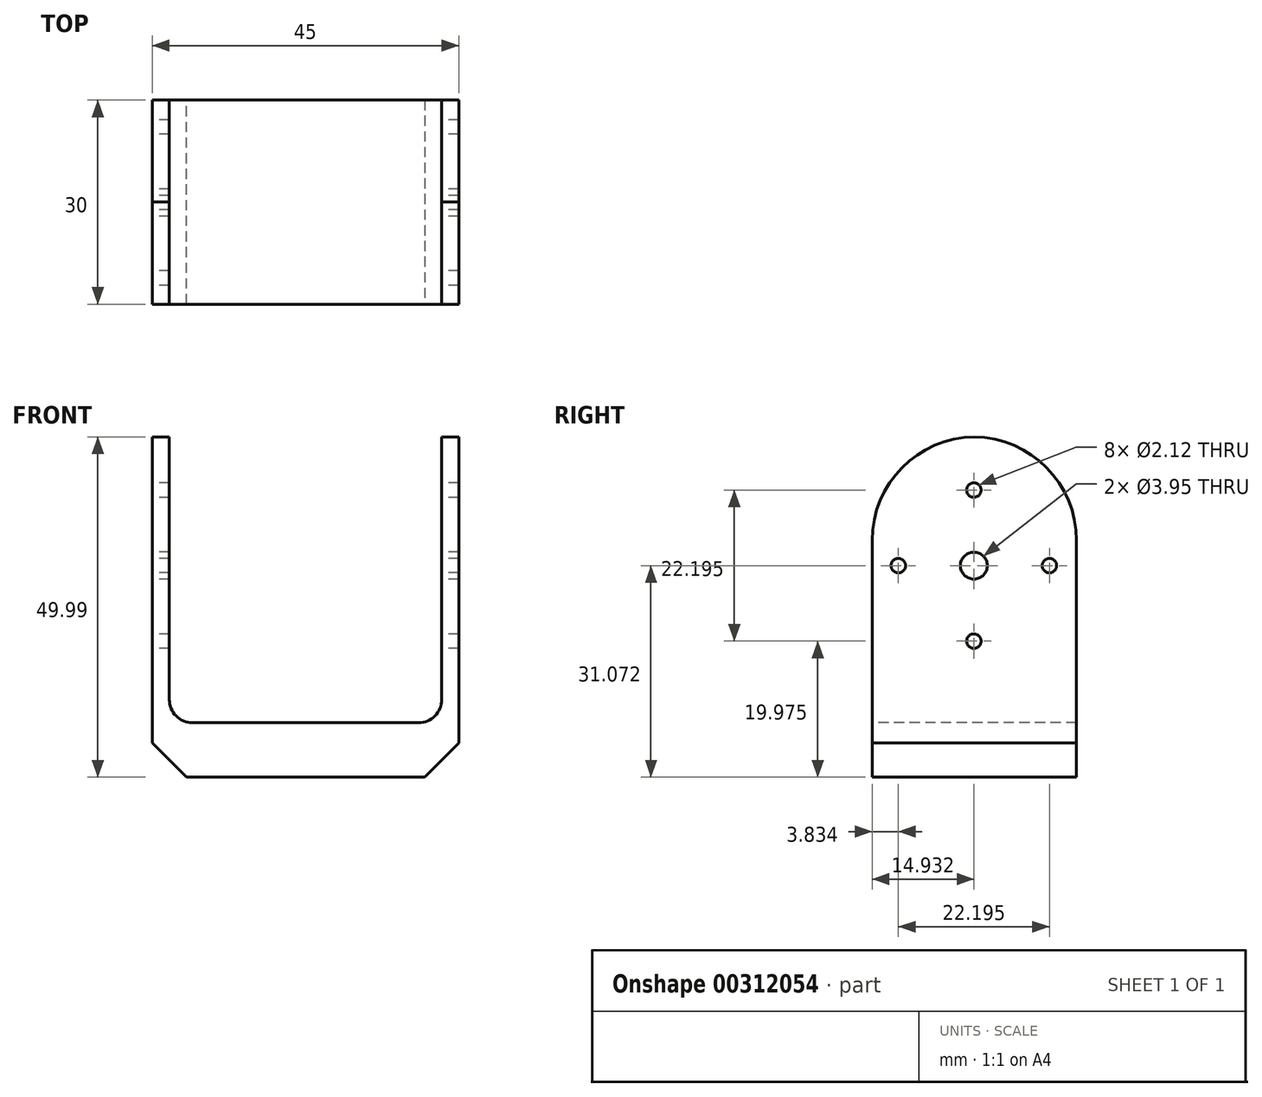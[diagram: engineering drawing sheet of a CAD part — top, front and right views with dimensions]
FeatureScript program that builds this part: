
annotation { "Feature Type Name" : "Feature", "Feature Type Description" : "" }
export const myFeature = defineFeature(function(context is Context, id is Id, definition is map)
    precondition{}
    {
        {
            var Q0;
            Q0=qCreatedBy(makeId("Front.planeOp"),FACE);
            var sketch = newSketch(context, id + "F0", { "sketchPlane" : qUnion([Q0])});
            skLineSegment(sketch, "E0.bottom", {"start": v(-16.8, 31.56) * mm, "end": v(28.2, 31.56) * mm});
            skLineSegment(sketch, "E0.top", {"start": v(-16.8, -18.44) * mm, "end": v(28.2, -18.44) * mm});
            skLineSegment(sketch, "E0.left", {"start": v(-16.8, 31.56) * mm, "end": v(-16.8, -18.44) * mm});
            skLineSegment(sketch, "E0.right", {"start": v(28.2, 31.56) * mm, "end": v(28.2, -18.44) * mm});
            skSolve(sketch);
        }
        {
            var Q0;
            Q0 = qSketchRegion(id + "F0", true);
            extrude(context, id + "F1", {"entities" : qUnion([Q0]), "depth" : 30 * mm});
        }
        {
            var Q0;
            Q0=makeQuery(id+"F1.opExtrude","CAP_FACE",FACE,{"disambiguationData":[OSD([sQuery(id+"F0.wireOp",EDGE,"E0.bottom"),sQuery(id+"F0.wireOp",EDGE,"E0.top"),sQuery(id+"F0.wireOp",EDGE,"E0.left"),sQuery(id+"F0.wireOp",EDGE,"E0.right")])],"isStart":false});
            var sketch = newSketch(context, id + "F2", { "sketchPlane" : qUnion([Q0])});
            skLineSegment(sketch, "E1.bottom", {"start": v(-14.3, 31.56) * mm, "end": v(25.7, 31.56) * mm, "construction": true});
            skLineSegment(sketch, "E1.top", {"start": v(-14.3, -10.44) * mm, "end": v(25.7, -10.44) * mm, "construction": true});
            skLineSegment(sketch, "E1.left", {"start": v(-14.3, 31.56) * mm, "end": v(-14.3, -10.44) * mm, "construction": true});
            skLineSegment(sketch, "E1.right", {"start": v(25.7, 31.56) * mm, "end": v(25.7, -10.44) * mm, "construction": true});
            skLineSegment(sketch, "E2.bottom", {"start": v(-14.3, 31.56) * mm, "end": v(25.7, 31.56) * mm});
            skLineSegment(sketch, "E2.top", {"start": v(-14.3, -10.44) * mm, "end": v(25.7, -10.44) * mm});
            skLineSegment(sketch, "E2.left", {"start": v(-14.3, 31.56) * mm, "end": v(-14.3, -10.44) * mm});
            skLineSegment(sketch, "E2.right", {"start": v(25.7, 31.56) * mm, "end": v(25.7, -10.44) * mm});
            skSolve(sketch);
        }
        {
            var Q0;
            Q0 = qSketchRegion(id + "F2", true);
            extrude(context, id + "F3", {"entities" : qUnion([Q0]), "operationType" : NewBodyOperationType.REMOVE, "endBound" : BoundingType.THROUGH_ALL, "oppositeDirection" : true, "depth" : 25 * mm});
        }
        {
            var Q0;
            {var subQ0=sQuery(id+"F0.wireOp",EDGE,"E0.bottom");var subQ1=sQuery(id+"F0.wireOp",EDGE,"E0.left");Q0=makeQuery(id+"F3.boolean.opBoolean","SPLIT",EDGE,{"disambiguationData":[TD([makeQuery(id+"F1.opExtrude","SWEPT_FACE",FACE,{"disambiguationData":[OSD([subQ1])]})])],"derivedFrom":makeQuery(id+"F1.opExtrude","CAP_EDGE",EDGE,{"disambiguationData":[OSD([subQ0])],"isStart":true})});}
            var Q1;
            {var subQ0=sQuery(id+"F0.wireOp",EDGE,"E0.bottom");var subQ1=sQuery(id+"F0.wireOp",EDGE,"E0.left");Q1=makeQuery(id+"F3.boolean.opBoolean","SPLIT",EDGE,{"disambiguationData":[TD([makeQuery(id+"F1.opExtrude","SWEPT_FACE",FACE,{"disambiguationData":[OSD([subQ1])]})])],"derivedFrom":makeQuery(id+"F1.opExtrude","CAP_EDGE",EDGE,{"disambiguationData":[OSD([subQ0])],"isStart":false})});}
            var Q2;
            {var subQ0=sQuery(id+"F0.wireOp",EDGE,"E0.bottom");var subQ1=sQuery(id+"F0.wireOp",EDGE,"E0.right");Q2=makeQuery(id+"F3.boolean.opBoolean","SPLIT",EDGE,{"disambiguationData":[TD([makeQuery(id+"F1.opExtrude","SWEPT_FACE",FACE,{"disambiguationData":[OSD([subQ1])]})])],"derivedFrom":makeQuery(id+"F1.opExtrude","CAP_EDGE",EDGE,{"disambiguationData":[OSD([subQ0])],"isStart":false})});}
            var Q3;
            {var subQ0=sQuery(id+"F0.wireOp",EDGE,"E0.bottom");var subQ1=sQuery(id+"F0.wireOp",EDGE,"E0.right");Q3=makeQuery(id+"F3.boolean.opBoolean","SPLIT",EDGE,{"disambiguationData":[TD([makeQuery(id+"F1.opExtrude","SWEPT_FACE",FACE,{"disambiguationData":[OSD([subQ1])]})])],"derivedFrom":makeQuery(id+"F1.opExtrude","CAP_EDGE",EDGE,{"disambiguationData":[OSD([subQ0])],"isStart":true})});}
            fillet(context, id + "F4", {"entities" : qUnion([Q0, Q1, Q2, Q3]), "radius" : 15.2 * mm, "tangentPropagation" : true, "allowEdgeOverflow" : false});
        }
        {
            var Q0;
            Q0=makeQuery(id+"F3.boolean.opBoolean","COPY",EDGE,{"derivedFrom":makeQuery(id+"F3.opExtrude","SWEPT_EDGE",EDGE,{"disambiguationData":[OSD([sQuery(id+"F2.wireOp",EDGE,"E2.top"),sQuery(id+"F2.wireOp",EDGE,"E2.left")])]})});
            var Q1;
            Q1=makeQuery(id+"F3.boolean.opBoolean","COPY",EDGE,{"derivedFrom":makeQuery(id+"F3.opExtrude","SWEPT_EDGE",EDGE,{"disambiguationData":[OSD([sQuery(id+"F2.wireOp",EDGE,"E2.top"),sQuery(id+"F2.wireOp",EDGE,"E2.right")])]})});
            fillet(context, id + "F5", {"entities" : qUnion([Q0, Q1]), "radius" : 3.38 * mm, "tangentPropagation" : true, "allowEdgeOverflow" : false});
        }
        {
            var Q0;
            Q0=makeQuery(id+"F1.opExtrude","SWEPT_EDGE",EDGE,{"disambiguationData":[OSD([sQuery(id+"F0.wireOp",EDGE,"E0.top"),sQuery(id+"F0.wireOp",EDGE,"E0.left")])]});
            var Q1;
            Q1=makeQuery(id+"F1.opExtrude","SWEPT_EDGE",EDGE,{"disambiguationData":[OSD([sQuery(id+"F0.wireOp",EDGE,"E0.top"),sQuery(id+"F0.wireOp",EDGE,"E0.right")])]});
            chamfer(context, id + "F6", {"entities" : qUnion([Q0, Q1]), "width" : 5 * mm, "tangentPropagation" : true});
        }
        {
            var Q0;
            Q0=makeQuery(id+"F1.opExtrude","SWEPT_FACE",FACE,{"disambiguationData":[OSD([sQuery(id+"F0.wireOp",EDGE,"E0.left")])]});
            var sketch = newSketch(context, id + "F7", { "sketchPlane" : qUnion([Q0])});
            skCircle(sketch, "E3", {"center": v(3.97, 12.63) * mm, "radius": 1.06 * mm});
            skCircle(sketch, "E4", {"center": v(15.07, 23.73) * mm, "radius": 1.06 * mm});
            skCircle(sketch, "E5", {"center": v(26.17, 12.63) * mm, "radius": 1.06 * mm});
            skCircle(sketch, "E6", {"center": v(15.07, 1.53) * mm, "radius": 1.06 * mm});
            skCircle(sketch, "E7", {"center": v(15.07, 12.63) * mm, "radius": 1.97 * mm});
            skLineSegment(sketch, "E8", {"start": v(15.07, 12.63) * mm, "end": v(15.07, 27.5) * mm, "construction": true});
            skLineSegment(sketch, "E9", {"start": v(15.07, 12.63) * mm, "end": v(15.07, -6.42) * mm, "construction": true});
            skSolve(sketch);
        }
        {
            var Q0;
            Q0 = qSketchRegion(id + "F7", true);
            extrude(context, id + "F8", {"entities" : qUnion([Q0]), "operationType" : NewBodyOperationType.REMOVE, "endBound" : BoundingType.THROUGH_ALL, "oppositeDirection" : true, "depth" : 25 * mm});
        }
    });
